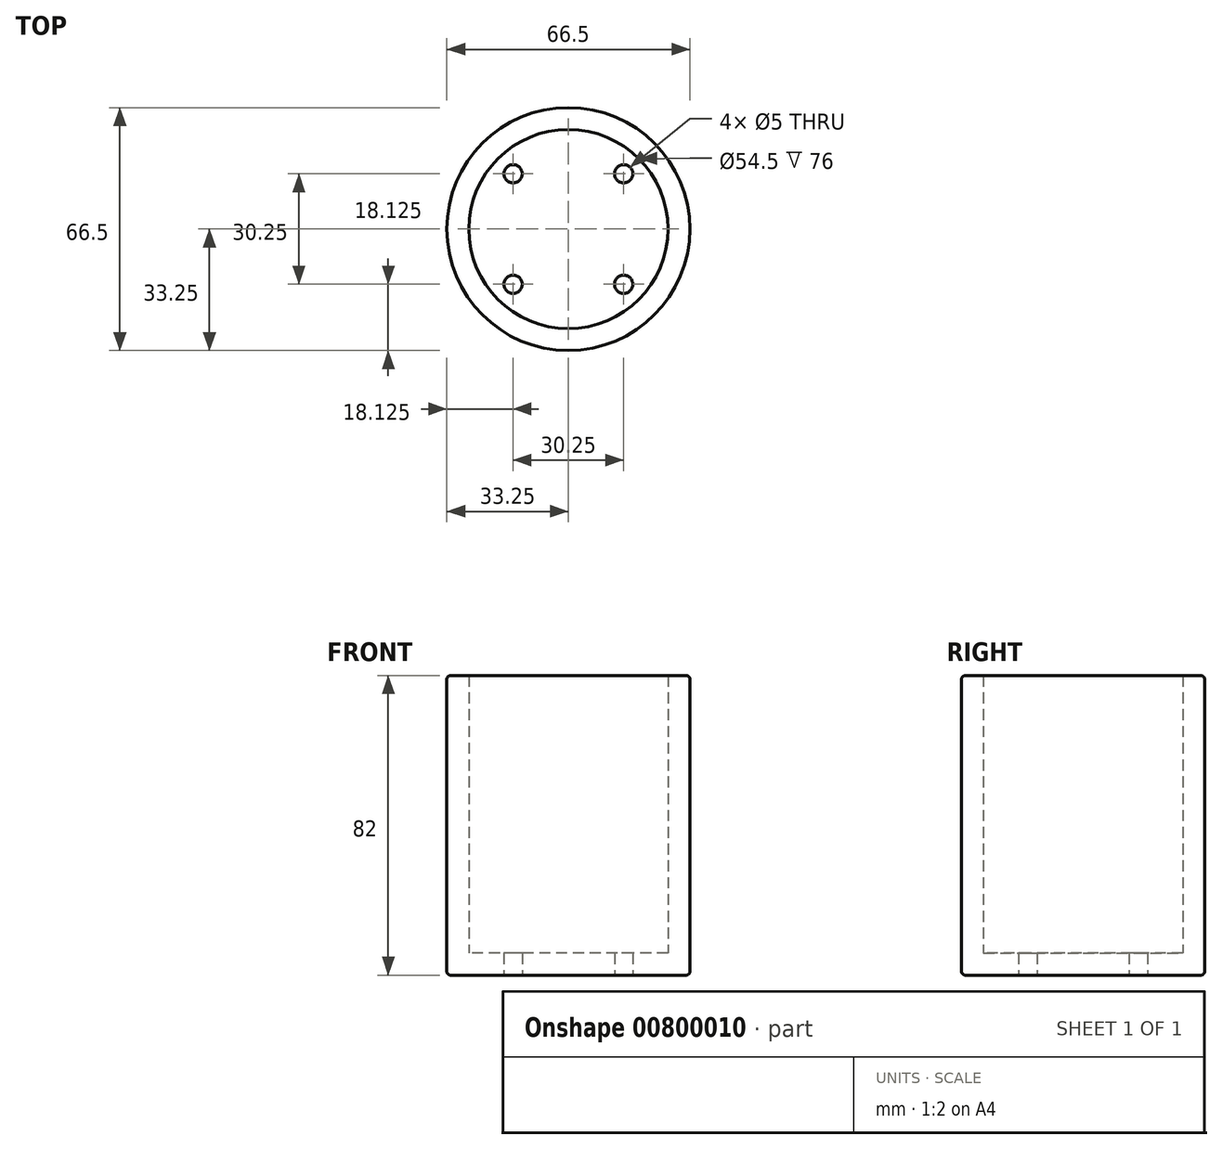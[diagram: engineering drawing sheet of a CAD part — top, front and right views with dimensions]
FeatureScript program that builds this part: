
annotation { "Feature Type Name" : "Feature", "Feature Type Description" : "" }
export const myFeature = defineFeature(function(context is Context, id is Id, definition is map)
    precondition{}
    {
        {
            assignVariable(context, id + "F0", {"name" : "Wall_thickness", "anyValue" : 6 * mm});
        }
        {
            assignVariable(context, id + "F1", {"name" : "Brim_height", "anyValue" : 22 * mm});
        }
        {
            assignVariable(context, id + "F2", {"name" : "Wall_height", "anyValue" : 65 * mm});
        }
        {
            var Q0;
            Q0=qCreatedBy(makeId("Top.planeOp"),FACE);
            var sketch = newSketch(context, id + "F3", { "sketchPlane" : qUnion([Q0])});
            skCircle(sketch, "E0", {"center": v(0, 0) * mm, "radius": 33.25 * mm});
            skLineSegment(sketch, "E1.bottom", {"start": v(15.13, 15.12) * mm, "end": v(-15.12, 15.12) * mm, "construction": true});
            skLineSegment(sketch, "E1.top", {"start": v(15.12, -15.12) * mm, "end": v(-15.13, -15.12) * mm, "construction": true});
            skLineSegment(sketch, "E1.left", {"start": v(15.13, 15.12) * mm, "end": v(15.12, -15.12) * mm, "construction": true});
            skLineSegment(sketch, "E1.right", {"start": v(-15.13, 15.12) * mm, "end": v(-15.13, -15.12) * mm, "construction": true});
            skSolve(sketch);
        }
        {
            var Q0;
            Q0=makeQuery(id+"F3.imprint","IMPRINT",FACE,{"disambiguationData":[TD([[makeQuery(id+"F3.imprint","IMPRINT",EDGE,{"derivedFrom":sQuery(id+"F3.wireOp",EDGE,"E0")}),1.0]])]});
            var Q1;
            Q1 = qConstructionFilter(qBodyType(qCreatedBy(id + "F3" ,EDGE), BodyType.WIRE), ConstructionObject.NO);
            extrude(context, id + "F4", {"entities" : qUnion([Q0]), "surfaceEntities" : qUnion([Q1]), "depth" : getVariable(context, 'Wall_thickness'), "offsetDistance" : 25.4 * mm});
        }
        {
            var Q0;
            Q0=makeQuery(id+"F4.opExtrude","CAP_FACE",FACE,{"disambiguationData":[OSD([sQuery(id+"F3.wireOp",EDGE,"E0")])],"isStart":false});
            var sketch = newSketch(context, id + "F5", { "sketchPlane" : qUnion([Q0])});
            skCircle(sketch, "E2", {"center": v(0, 0) * mm, "radius": 33.25 * mm});
            skCircle(sketch, "E3", {"center": v(0, 0) * mm, "radius": 27.25 * mm});
            skSolve(sketch);
        }
        {
            var Q0;
            Q0=makeQuery(id+"F5.imprint","IMPRINT",FACE,{"disambiguationData":[TD([[makeQuery(id+"F5.imprint","IMPRINT",EDGE,{"derivedFrom":sQuery(id+"F5.wireOp",EDGE,"E2")}),1.0]])]});
            extrude(context, id + "F6", {"entities" : qUnion([Q0]), "operationType" : NewBodyOperationType.ADD, "depth" : getVariable(context, 'Wall_height') + (getVariable(context, 'Brim_height')) / 2, "offsetDistance" : 25 * mm});
        }
        {
            var Q0;
            Q0=sQuery(id+"F3.wireOp",VERTEX,"E1.bottom.end");
            var Q1;
            Q1=sQuery(id+"F3.wireOp",VERTEX,"E1.bottom.start");
            var Q2;
            Q2=sQuery(id+"F3.wireOp",VERTEX,"E1.top.start");
            var Q3;
            Q3=sQuery(id+"F3.wireOp",VERTEX,"E1.top.end");
            var Q4;
            Q4=makeQuery(id+"F4.opExtrude","SWEPT_BODY",BODY,{"disambiguationData":[OSD([sQuery(id+"F3.wireOp",EDGE,"E0")])]});
            hole(context, id + "F7", {"style" : HoleStyle.SIMPLE, "endStyle" : HoleEndStyle.THROUGH, "oppositeDirection" : true, "holeDiameter" : 5 * mm, "majorDiameter" : 5 * mm, "isTappedThrough" : true, "tappedDepth" : 12 * mm, "tapClearance" : 3, "locations" : qUnion([Q0, Q1, Q2, Q3]), "scope" : qUnion([Q4])});
        }
        {
            var Q0;
            Q0=makeQuery(id+"F4.opExtrude","CAP_EDGE",EDGE,{"disambiguationData":[OSD([sQuery(id+"F3.wireOp",EDGE,"E0")])],"isStart":true});
            var Q1;
            Q1=makeQuery(id+"F6.opExtrude","CAP_EDGE",EDGE,{"disambiguationData":[OSD([sQuery(id+"F5.wireOp",EDGE,"E2")])],"isStart":false});
            fillet(context, id + "F8", {"entities" : qUnion([Q0, Q1]), "radius" : 1 * mm, "tangentPropagation" : true, "allowEdgeOverflow" : false});
        }
    });
